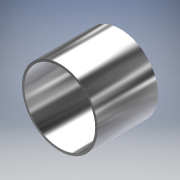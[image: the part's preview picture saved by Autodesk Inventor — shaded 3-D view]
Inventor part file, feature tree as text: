
AUTODESK INVENTOR PART (.ipt)
format: ipt  version: 2017 (Build 210142000, 142)  size: 126,976 bytes
history: native  units: in
note: dims shown in document units (in); Inventor stores cm internally (conversion verified against a paired STEP export)
features: extrude x1, sketch x1
ambient origin geometry x8: Origin, YZ Plane, XZ Plane, XY Plane, X Axis, Y Axis, Z Axis, Center Point
bodies: Solid1 (feature_tree)
feature tree (2):
  extrude  "Extrusion1"  Depth=3.2in
  sketch  "Sketch1"  dims[d0=4.0in d1=0.125in d2=3.2in d3=0.0in]
